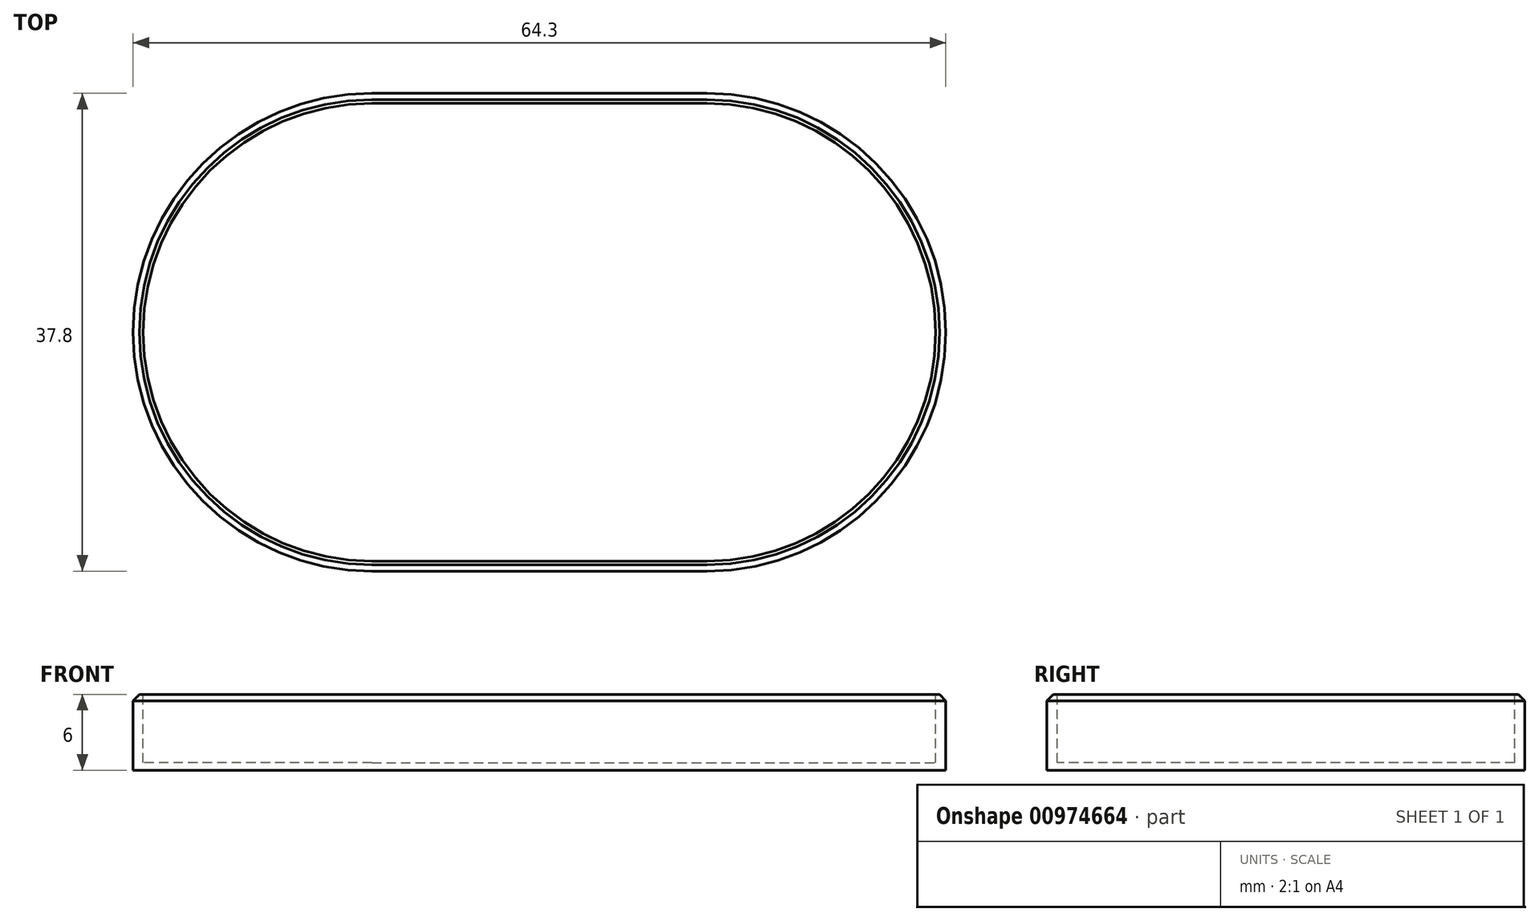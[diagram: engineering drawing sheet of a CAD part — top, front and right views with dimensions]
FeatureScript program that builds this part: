
annotation { "Feature Type Name" : "Feature", "Feature Type Description" : "" }
export const myFeature = defineFeature(function(context is Context, id is Id, definition is map)
    precondition{}
    {
        {
            var Q0;
            Q0=qCreatedBy(makeId("Top.planeOp"),FACE);
            var sketch = newSketch(context, id + "F0", { "sketchPlane" : qUnion([Q0])});
            skLineSegment(sketch, "E0.bottom", {"start": v(-13.25, 18.9) * mm, "end": v(13.25, 18.9) * mm});
            skLineSegment(sketch, "E0.top", {"start": v(-13.25, -18.9) * mm, "end": v(13.25, -18.9) * mm});
            skLineSegment(sketch, "E0.left", {"start": v(-32.15, 0) * mm, "end": v(-32.15, 0) * mm});
            skLineSegment(sketch, "E0.right", {"start": v(32.15, 0) * mm, "end": v(32.15, 0) * mm});
            skPoint(sketch, "E1.visualSharp", {"position": v(-32.15, 18.9) * mm});
            skArc(sketch, "E1.filletArc", {"start": v(-13.25, 18.9) * mm, "mid": v(-26.61, 13.36) * mm, "end": v(-32.15, 0) * mm});
            skPoint(sketch, "E2.visualSharp", {"position": v(-32.15, -18.9) * mm});
            skArc(sketch, "E2.filletArc", {"start": v(-32.15, 0) * mm, "mid": v(-26.61, -13.36) * mm, "end": v(-13.25, -18.9) * mm});
            skPoint(sketch, "E3.visualSharp", {"position": v(32.15, -18.9) * mm});
            skArc(sketch, "E3.filletArc", {"start": v(13.25, -18.9) * mm, "mid": v(26.61, -13.36) * mm, "end": v(32.15, 0) * mm});
            skPoint(sketch, "E4.visualSharp", {"position": v(32.15, 18.9) * mm});
            skArc(sketch, "E4.filletArc", {"start": v(32.15, 0) * mm, "mid": v(26.61, 13.36) * mm, "end": v(13.25, 18.9) * mm});
            skSolve(sketch);
        }
        {
            var Q0;
            Q0 = qSketchRegion(id + "F0", true);
            extrude(context, id + "F1", {"entities" : qUnion([Q0]), "depth" : 6 * mm, "offsetDistance" : 25 * mm});
        }
        {
            var Q0;
            Q0=makeQuery(id+"F1.opExtrude","CAP_FACE",FACE,{"disambiguationData":[OSD([sQuery(id+"F0.wireOp",EDGE,"E0.bottom"),sQuery(id+"F0.wireOp",EDGE,"E0.top"),sQuery(id+"F0.wireOp",EDGE,"E1.filletArc"),sQuery(id+"F0.wireOp",EDGE,"E2.filletArc"),sQuery(id+"F0.wireOp",EDGE,"E3.filletArc"),sQuery(id+"F0.wireOp",EDGE,"E4.filletArc")])],"isStart":false});
            var sketch = newSketch(context, id + "F2", { "sketchPlane" : qUnion([Q0])});
            skArc(sketch, "E5.0", {"start": v(-13.25, 18.1) * mm, "mid": v(-31.35, 0) * mm, "end": v(-13.25, -18.1) * mm});
            skLineSegment(sketch, "E6.0", {"start": v(-13.25, 18.1) * mm, "end": v(13.25, 18.1) * mm});
            skArc(sketch, "E7.0", {"start": v(13.25, -18.1) * mm, "mid": v(31.35, 0) * mm, "end": v(13.25, 18.1) * mm});
            skLineSegment(sketch, "E8.0", {"start": v(-13.25, -18.1) * mm, "end": v(13.25, -18.1) * mm});
            skSolve(sketch);
        }
        {
            var Q0;
            Q0 = qSketchRegion(id + "F2", true);
            extrude(context, id + "F3", {"entities" : qUnion([Q0]), "operationType" : NewBodyOperationType.REMOVE, "oppositeDirection" : true, "depth" : 5.4 * mm, "offsetDistance" : 25 * mm});
        }
        {
            var Q0;
            Q0=makeQuery(id+"F1.opExtrude","CAP_EDGE",EDGE,{"disambiguationData":[OSD([sQuery(id+"F0.wireOp",EDGE,"E1.filletArc"),sQuery(id+"F0.wireOp",EDGE,"E2.filletArc")])],"isStart":false});
            chamfer(context, id + "F4", {"entities" : qUnion([Q0]), "width" : 0.5 * mm, "tangentPropagation" : true});
        }
    });
